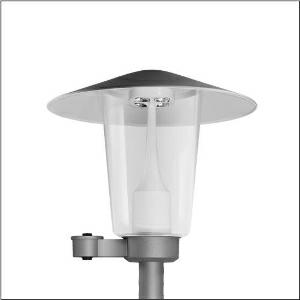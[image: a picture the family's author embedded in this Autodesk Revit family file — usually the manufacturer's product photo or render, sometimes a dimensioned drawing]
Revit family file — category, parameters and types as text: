
# Revit family: pilzleuchte_iq___st1_2a_5xa5235ey14h000022_5405
name_source: partatom
category: Lighting Fixtures
units: mm (PartAtom-declared; Revit-internal decimal feet)

## family parameters
Cut with Voids When Loaded = No
Host = Face
Light Source = No
Part Type = Normal
Room Calculation Point = No
Round Connector Dimension = Use Diameter
Shared = No

## types (1)
- --- (1 x LED, 1550 lm, 10.7 W, 3000K)
    Apparent Load = 11 VA
    CIE Flux Codes = 24 61 93 98 100
    Color Rendering = 70
    Color Temperature = 3000K
    Default Elevation = 1800 mm
    Description = Mushroom Luminaire iQ, mast luminaire, Module 540 iQ-SR, primary light control with 3 zone facetted reflector, of plastic, silver coated, highly specular, structured, primary optical cover: cover, of PMMA, transparent, light distribution: ST1.2a, light emission: direct distribution, primary light characteristic: asymmetric, installation type: post-top, LED, High Power LED, rated luminous flux: 1.550lm, luminous efficacy: 145lm/W, light colour: 730, colour temperature: 3000K, control gear: iQ-Street Remote, D4i with power reduction, control: optimised constant luminous flux control (CLO 2.0), Desk-Remote (wireless, voltage-free reading and setting of iQ features in the workshop via application-optimized NFC function/RFID function), Light-Fading, Smart-Wire, Night-Set, Lumen-Switch, Temp-Guard, Auto-Match, Street-Remote, pre-setting: logarithmic dimming characteristic, with terminal, 6-pole, max. 2.5mm², mains connection: 230..240V, AC, 50/60Hz, connection cable pre-assembled, cable length: 5,5m, wiring characteristics: H07RN-F, start of lifetime: 11W, end of service life: 11W, reduction: 6W, luminaire housing, upper part, of glass-fibre reinforced polyester, coated, Siteco® metallic grey (DB 702S), diameter: 650mm, height: 586mm, spigot size: d x l = 76 x 70mm (post-top) | with reducer (optional accessory) 60 x 70mm, mounting height: 3..5m, post-top mast mounting element, of diecast aluminium, coated, Siteco® metallic grey (DB 702S), Module 540 iQ-SR, traffic white (RAL 9016), equipment: standard, Smart Interface below and above, protection rating (complete): IP65, insulation class (complete): insulation class II (safety insulation), certification: CE, ENEC, VDE, packaging unit: 1 piece

Light Distribution: ST1.2a
    Height = 586 mm
    Lamp = 1 x LED
    Lamp Light Flux = 1550 lm
    Lamp Power = 10.7 W
    Lamp count = 1
    Length = 650 mm
    Luminous efficacy = 145 lm/W
    Manufacturer = Siteco
    ModVariant = No
    Model = 5XA5235EY14H000022
    Number of Poles = 1
    OnlyDefault = Yes
    Power Factor = 1
    Product Name = Pilzleuchte iQ | ST1.2a
    Product group = mast luminaire | pylon top
    ProductGroupID = 6100
    Protection Class = Protection class II
    Protection Degree = IP 65
    RLX_Detail_Level = 1
    RLX_Emergency_Light_Flux = 0 lm
    RLX_Emergency_Type = 0
    RLX_Emergency_Type_DB = No
    RlxData = <blob elided: 51653 chars, md5=4dd4410b>
    Socket = socket
    Standby Power = 0 W
    System Light Flux = 1550 lm
    System Power = 11 W
    Type Comments = factory setting: luminous flux: 100 % | dim-lin: 254 | 419 mA
    Type Image = l_1006957.jpg
    URL = http://relux.com
    VarID = @adj_108301
    Voltage = 0 V
    Weight = 0.00 kg
    Width = 0 mm  [stored 0 ft]

note: [stored X ft] marks values corroborated as IEEE doubles in the binary element streams (Revit-internal decimal feet)

## geometry (parser evidence)
native form markers: Blend x4, Sweep x13
no freeform markers — native parametric forms only
